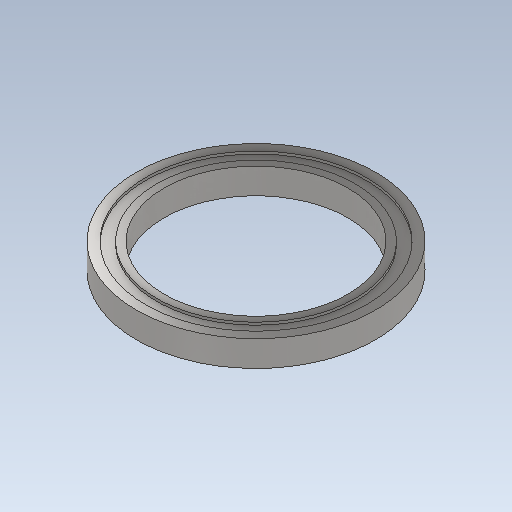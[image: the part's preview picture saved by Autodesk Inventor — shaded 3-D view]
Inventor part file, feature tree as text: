
AUTODESK INVENTOR PART (.ipt)
format: ipt  version: 2020 (Build 240168000, 168)  size: 144,896 bytes
history: native  units: mm
features: extrude x3, sketch x3
ambient origin geometry x8: Origin, YZ Plane, XZ Plane, XY Plane, X Axis, Y Axis, Z Axis, Center Point
bodies: Solid1 (feature_tree)
feature tree (6):
  extrude  "Extrusion1"  Depth=65.0mm
  extrude  "Extrusion2"  Depth=7.0mm
  extrude  "Extrusion3"  Depth=0.7mm TaperAngle=0.0deg
  sketch  "Sketch1"  dims[d0=50.0mm d1=65.0mm]
  sketch  "Sketch2"  dims[d2=7.0mm d3=0.0mm d4=54.0mm]
  sketch  "Sketch3"  dims[d5=60.0mm d6=0.7mm d7=0.0mm d8=0.7mm d9=0.0mm]
